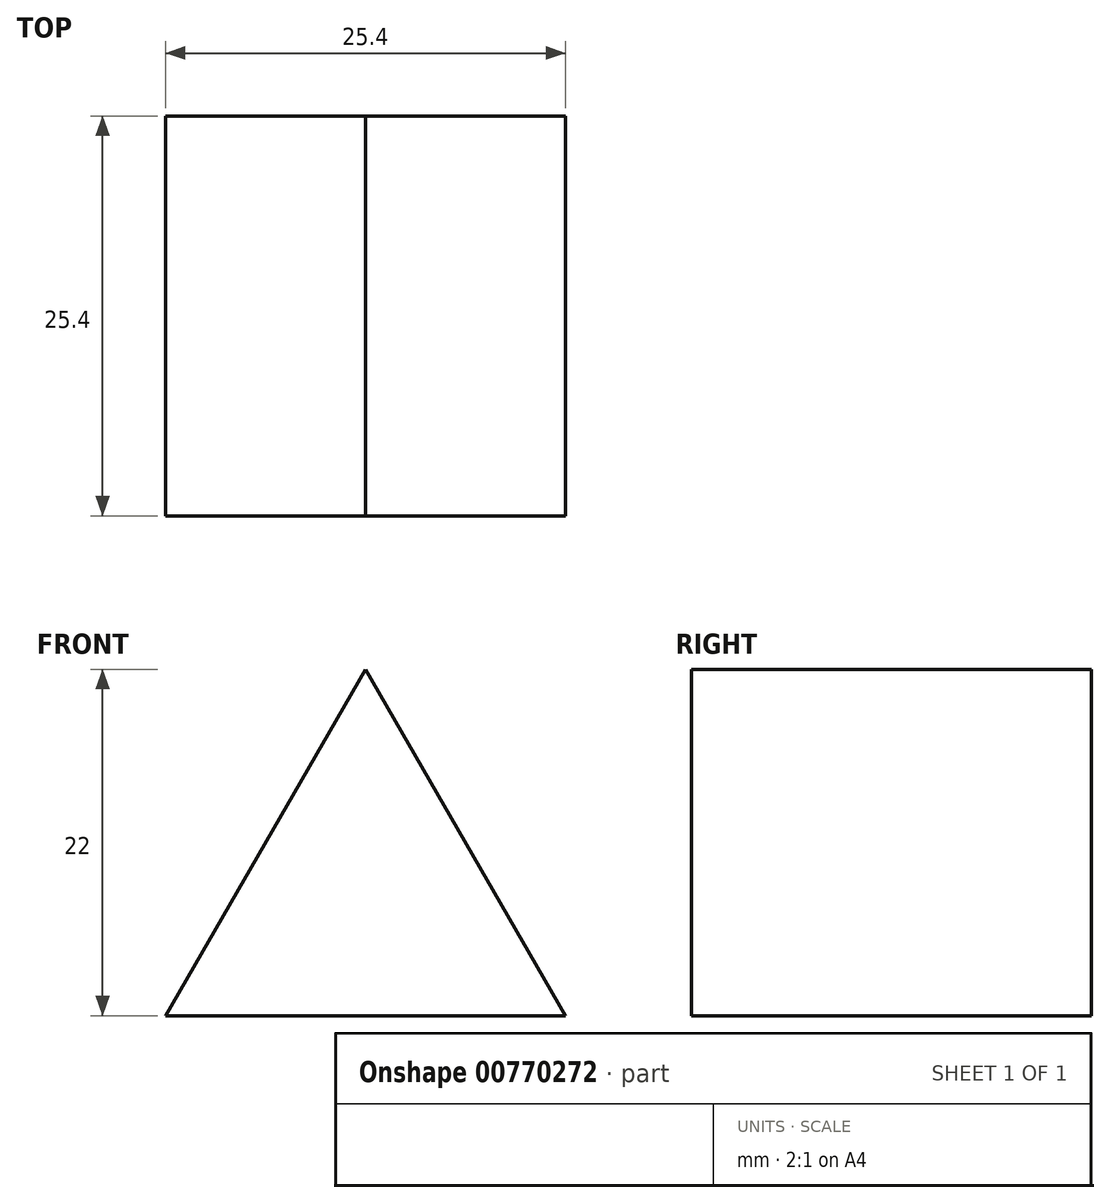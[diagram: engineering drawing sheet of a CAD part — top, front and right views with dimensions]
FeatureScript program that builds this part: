
annotation { "Feature Type Name" : "Feature", "Feature Type Description" : "" }
export const myFeature = defineFeature(function(context is Context, id is Id, definition is map)
    precondition{}
    {
        {
            var Q0;
            Q0=qCreatedBy(makeId("Front.planeOp"),FACE);
            var sketch = newSketch(context, id + "F0", { "sketchPlane" : qUnion([Q0])});
            skLineSegment(sketch, "E0", {"start": v(0, 0) * mm, "end": v(-25.4, 0) * mm});
            skLineSegment(sketch, "E1", {"start": v(-25.4, 0) * mm, "end": v(-12.7, 22) * mm});
            skLineSegment(sketch, "E2", {"start": v(-12.7, 22) * mm, "end": v(0, 0) * mm});
            skSolve(sketch);
        }
        {
            var Q0;
            Q0 = qSketchRegion(id + "F0", true);
            extrude(context, id + "F1", {"entities" : qUnion([Q0]), "depth" : 25.4 * mm, "offsetDistance" : 25.4 * mm});
        }
    });
